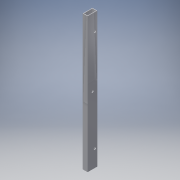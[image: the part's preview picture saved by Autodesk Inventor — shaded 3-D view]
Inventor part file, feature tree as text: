
AUTODESK INVENTOR PART (.ipt)
format: ipt  version: 2016 (Build 200138000, 138)  size: 134,144 bytes
history: native  units: in
note: dims shown in document units (in); Inventor stores cm internally (conversion verified against a paired STEP export)
features: extrude x2, sketch x2
ambient origin geometry x8: Origin, YZ Plane, XZ Plane, XY Plane, X Axis, Y Axis, Z Axis, Center Point
bodies: Solid1 (feature_tree)
feature tree (4):
  extrude  "Extrusion1"  Depth=2.0in
  extrude  "Extrusion2"  Depth=28.0in TaperAngle=0.0deg
  sketch  "Sketch1"  dims[d0=1.0in d1=2.0in]
  sketch  "Sketch2"  dims[d2=0.125in d3=28.0in d4=0.0in d5=0.5in d6=14.0in d7=1.0in d8=1.0in d9=0.0in d10=0.5in d11=1.5in d12=10.5in d13=0.5in d14=1.5in d15=10.5in]
